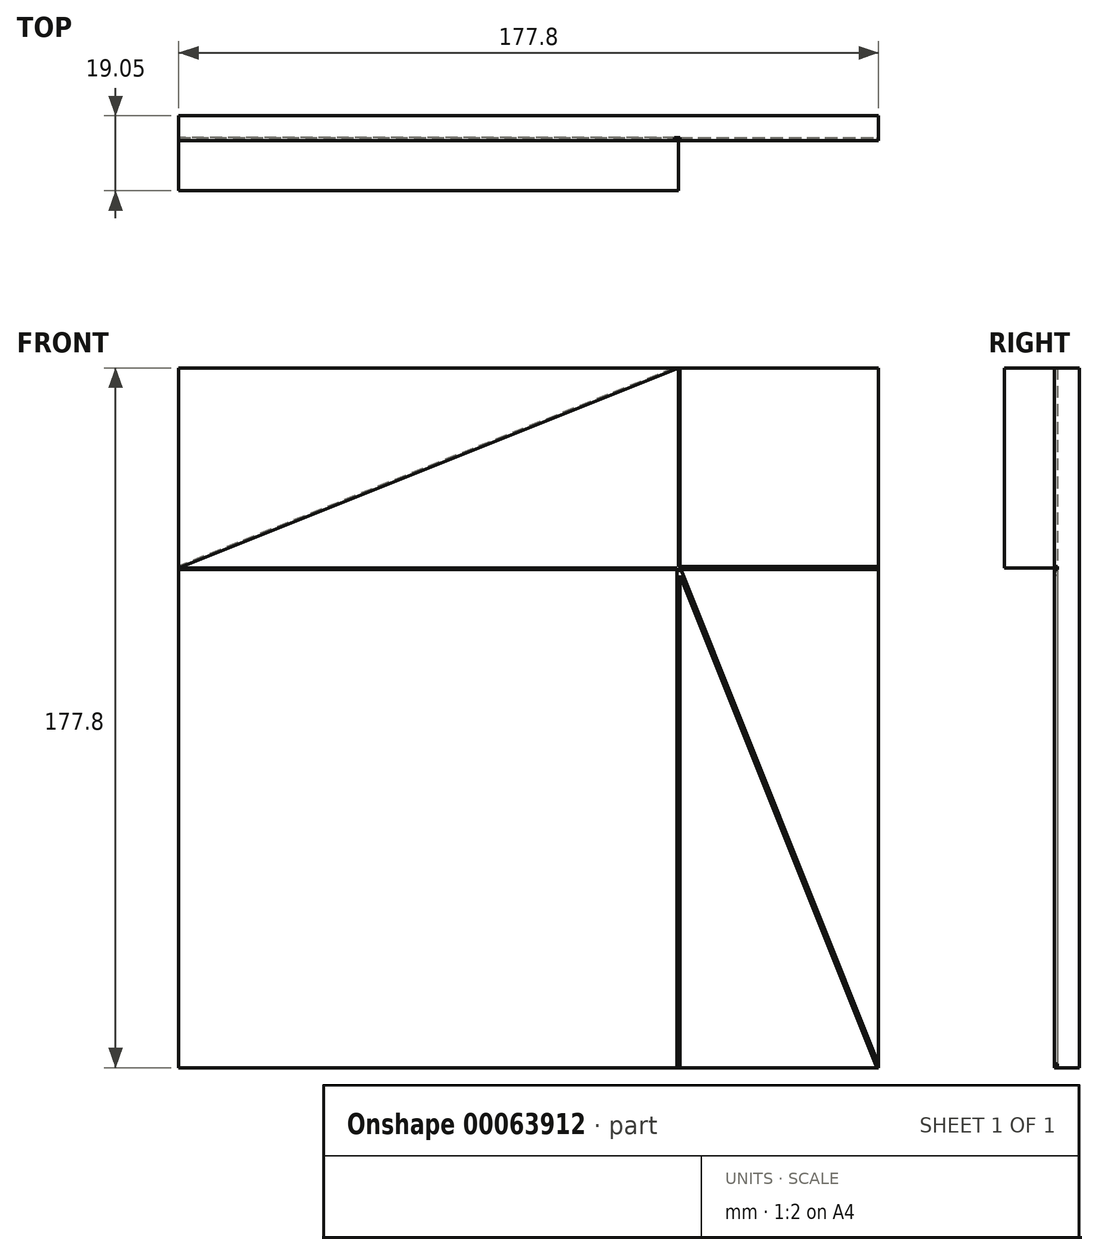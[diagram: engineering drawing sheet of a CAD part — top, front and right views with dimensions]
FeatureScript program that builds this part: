
annotation { "Feature Type Name" : "Feature", "Feature Type Description" : "" }
export const myFeature = defineFeature(function(context is Context, id is Id, definition is map)
    precondition{}
    {
        {
            var Q0;
            Q0=qCreatedBy(makeId("Front.planeOp"),FACE);
            var sketch = newSketch(context, id + "F0", { "sketchPlane" : qUnion([Q0])});
            skLineSegment(sketch, "E0.rect.bottom", {"start": v(88.9, 88.9) * mm, "end": v(-88.9, 88.9) * mm});
            skLineSegment(sketch, "E0.rect.top", {"start": v(88.9, -88.9) * mm, "end": v(-88.9, -88.9) * mm});
            skLineSegment(sketch, "E0.rect.left", {"start": v(88.9, 88.9) * mm, "end": v(88.9, -88.9) * mm});
            skLineSegment(sketch, "E0.rect.right", {"start": v(-88.9, 88.9) * mm, "end": v(-88.9, -88.9) * mm});
            skPoint(sketch, "E0.rect.middle", {"position": v(0, 0) * mm});
            skLineSegment(sketch, "E1", {"start": v(38.1, 88.9) * mm, "end": v(-88.9, 38.1) * mm});
            skLineSegment(sketch, "E2", {"start": v(-88.9, 88.9) * mm, "end": v(-88.9, 38.1) * mm, "construction": true});
            skLineSegment(sketch, "E3", {"start": v(38.1, 88.9) * mm, "end": v(88.9, 88.9) * mm, "construction": true});
            skSolve(sketch);
        }
        {
            var Q0;
            {var subQ1=sQuery(id+"F0.wireOp",EDGE,"E0.rect.top");Q0=makeQuery(id+"F0.imprint","IMPRINT",FACE,{"disambiguationData":[TD([[makeQuery(id+"F0.imprint","IMPRINT",EDGE,{"derivedFrom":subQ1}),-1.0]])]});}
            var Q1;
            {var subQ3=sQuery(id+"F0.wireOp",EDGE,"E1");Q1=makeQuery(id+"F0.imprint","IMPRINT",FACE,{"disambiguationData":[TD([[makeQuery(id+"F0.imprint","IMPRINT",EDGE,{"derivedFrom":subQ3}),-1.0]])]});}
            extrude(context, id + "F1", {"entities" : qUnion([Q0, Q1]), "oppositeDirection" : true, "depth" : 6.35 * mm});
        }
        {
            var Q0;
            {var subQ3=sQuery(id+"F0.wireOp",EDGE,"E1");Q0=makeQuery(id+"F0.imprint","IMPRINT",FACE,{"disambiguationData":[TD([[makeQuery(id+"F0.imprint","IMPRINT",EDGE,{"derivedFrom":subQ3}),-1.0]])]});}
            extrude(context, id + "F2", {"entities" : qUnion([Q0]), "depth" : 12.7 * mm});
        }
        {
            var Q0;
            {var subQ1=sQuery(id+"F0.wireOp",EDGE,"E0.rect.top");Q0=makeQuery(id+"F0.imprint","IMPRINT",FACE,{"disambiguationData":[TD([[makeQuery(id+"F0.imprint","IMPRINT",EDGE,{"derivedFrom":subQ1}),-1.0]])]});}
            var sketch = newSketch(context, id + "F3", { "sketchPlane" : qUnion([Q0])});
            skLineSegment(sketch, "E4.rect.bottom", {"start": v(-88.9, 88.9) * mm, "end": v(38.1, 88.9) * mm, "construction": true});
            skLineSegment(sketch, "E4.rect.top", {"start": v(-88.9, 38.1) * mm, "end": v(38.1, 38.1) * mm});
            skLineSegment(sketch, "E4.rect.left", {"start": v(-88.9, 88.9) * mm, "end": v(-88.9, 38.1) * mm, "construction": true});
            skLineSegment(sketch, "E4.rect.right", {"start": v(38.1, 88.9) * mm, "end": v(38.1, 38.1) * mm});
            skPoint(sketch, "E4.rect.middle", {"position": v(-25.4, 63.5) * mm});
            skLineSegment(sketch, "E5.rect.bottom", {"start": v(38.1, 38.1) * mm, "end": v(88.9, 38.1) * mm});
            skLineSegment(sketch, "E5.rect.top", {"start": v(38.1, -88.9) * mm, "end": v(88.9, -88.9) * mm, "construction": true});
            skLineSegment(sketch, "E5.rect.left", {"start": v(38.1, 38.1) * mm, "end": v(38.1, -88.9) * mm});
            skLineSegment(sketch, "E5.rect.right", {"start": v(88.9, 38.1) * mm, "end": v(88.9, -88.9) * mm, "construction": true});
            skPoint(sketch, "E5.rect.middle", {"position": v(63.5, -25.4) * mm});
            skLineSegment(sketch, "E6", {"start": v(38.1, 88.9) * mm, "end": v(-88.9, 38.1) * mm});
            skLineSegment(sketch, "E7", {"start": v(38.1, 38.1) * mm, "end": v(88.9, -88.9) * mm});
            skArc(sketch, "E8.0.startCap", {"start": v(37.72, 88.9) * mm, "mid": v(38.1, 89.28) * mm, "end": v(38.48, 88.9) * mm});
            skArc(sketch, "E8.0.endCap", {"start": v(38.48, 38.1) * mm, "mid": v(38.1, 37.72) * mm, "end": v(37.72, 38.1) * mm});
            skLineSegment(sketch, "E8.0.left", {"start": v(38.48, 88.9) * mm, "end": v(38.48, 38.1) * mm});
            skLineSegment(sketch, "E8.0.right", {"start": v(37.72, 88.9) * mm, "end": v(37.72, 38.1) * mm});
            skArc(sketch, "E8.1.startCap", {"start": v(38.1, 37.72) * mm, "mid": v(37.72, 38.1) * mm, "end": v(38.1, 38.48) * mm});
            skArc(sketch, "E8.1.endCap", {"start": v(88.9, 38.48) * mm, "mid": v(89.28, 38.1) * mm, "end": v(88.9, 37.72) * mm});
            skLineSegment(sketch, "E8.1.left", {"start": v(38.1, 38.48) * mm, "end": v(88.9, 38.48) * mm});
            skLineSegment(sketch, "E8.1.right", {"start": v(38.1, 37.72) * mm, "end": v(88.9, 37.72) * mm});
            skArc(sketch, "E8.2.startCap", {"start": v(37.75, 37.96) * mm, "mid": v(37.96, 38.45) * mm, "end": v(38.45, 38.24) * mm});
            skArc(sketch, "E8.2.endCap", {"start": v(89.25, -88.76) * mm, "mid": v(89.04, -89.25) * mm, "end": v(88.55, -89.04) * mm});
            skLineSegment(sketch, "E8.2.left", {"start": v(38.45, 38.24) * mm, "end": v(89.25, -88.76) * mm});
            skLineSegment(sketch, "E8.2.right", {"start": v(37.75, 37.96) * mm, "end": v(88.55, -89.04) * mm});
            skArc(sketch, "E8.3.startCap", {"start": v(37.72, 38.1) * mm, "mid": v(38.1, 38.48) * mm, "end": v(38.48, 38.1) * mm});
            skArc(sketch, "E8.3.endCap", {"start": v(38.48, -88.9) * mm, "mid": v(38.1, -89.28) * mm, "end": v(37.72, -88.9) * mm});
            skLineSegment(sketch, "E8.3.left", {"start": v(38.48, 38.1) * mm, "end": v(38.48, -88.9) * mm});
            skLineSegment(sketch, "E8.3.right", {"start": v(37.72, 38.1) * mm, "end": v(37.72, -88.9) * mm});
            skArc(sketch, "E8.4.startCap", {"start": v(-88.9, 37.72) * mm, "mid": v(-89.28, 38.1) * mm, "end": v(-88.9, 38.48) * mm});
            skArc(sketch, "E8.4.endCap", {"start": v(38.1, 38.48) * mm, "mid": v(38.48, 38.1) * mm, "end": v(38.1, 37.72) * mm});
            skLineSegment(sketch, "E8.4.left", {"start": v(-88.9, 38.48) * mm, "end": v(38.1, 38.48) * mm});
            skLineSegment(sketch, "E8.4.right", {"start": v(-88.9, 37.72) * mm, "end": v(38.1, 37.72) * mm});
            skArc(sketch, "E8.5.startCap", {"start": v(37.96, 89.25) * mm, "mid": v(38.45, 89.04) * mm, "end": v(38.24, 88.55) * mm});
            skArc(sketch, "E8.5.endCap", {"start": v(-88.76, 37.75) * mm, "mid": v(-89.25, 37.96) * mm, "end": v(-89.04, 38.45) * mm});
            skLineSegment(sketch, "E8.5.left", {"start": v(38.24, 88.55) * mm, "end": v(-88.76, 37.75) * mm});
            skLineSegment(sketch, "E8.5.right", {"start": v(37.96, 89.25) * mm, "end": v(-89.04, 38.45) * mm});
            skSolve(sketch);
        }
        {
            var Q0;
            Q0 = qSketchRegion(id + "F3", true);
            extrude(context, id + "F4", {"entities" : qUnion([Q0]), "operationType" : NewBodyOperationType.REMOVE, "oppositeDirection" : true, "depth" : 0.76 * mm});
        }
    });
